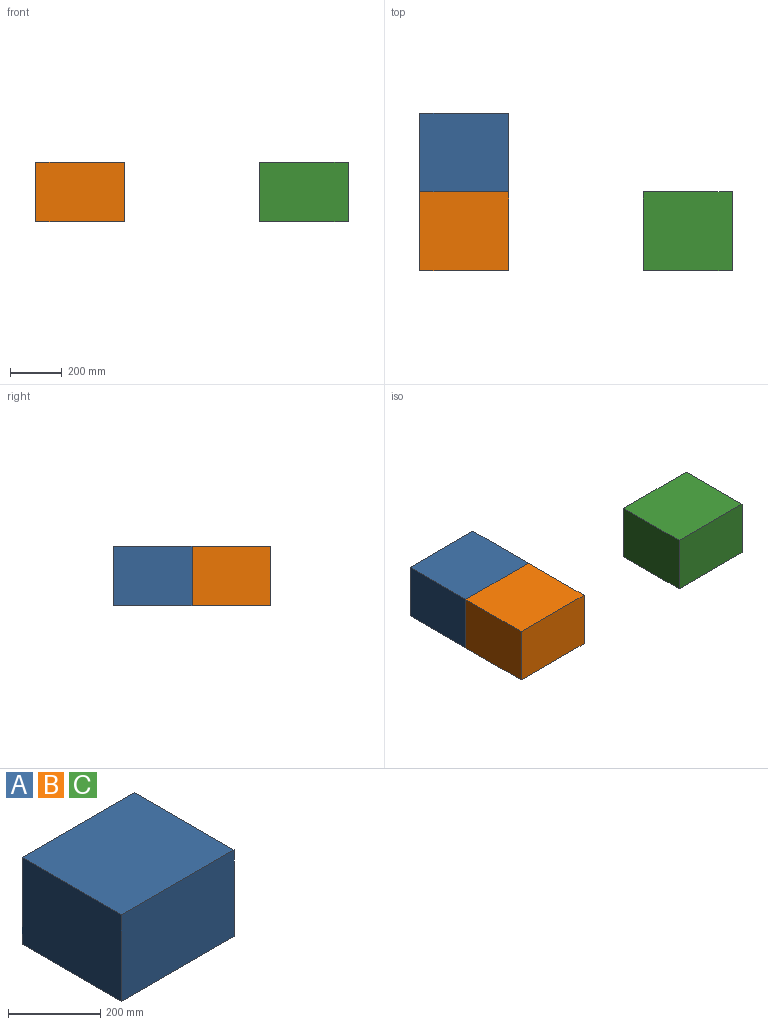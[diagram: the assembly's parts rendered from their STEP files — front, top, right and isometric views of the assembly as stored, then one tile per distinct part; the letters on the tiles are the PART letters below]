
ASSEMBLY  parts=3 mates=5
PART A: 6 faces, bbox 345x305x230 mm
  f0: plane 305x230mm, normal (-1,0,0), area 70150mm2, adj f1,f3,f4,f5
  f1: plane 345x230mm, normal (0,-1,0), area 79350mm2, adj f0,f2,f4,f5
  f2: plane 305x230mm, normal (1,0,0), area 70150mm2, adj f1,f3,f4,f5
  f3: plane 345x230mm, normal (0,1,0), area 79350mm2, adj f0,f2,f4,f5
  f4: plane 345x305mm, normal (0,0,1), area 105225mm2, adj f0,f1,f2,f3
  f5: plane 345x305mm, normal (0,0,-1), area 105225mm2, adj f0,f1,f2,f3
PART B: same geometry as A
PART C: same geometry as A
PLACE A t=(860.44,1794.7,-178.96)mm
PLACE B t=(860.44,1489.7,-178.96)mm
PLACE C t=(1726.91,1489.7,-178.96)mm
MATE planar A.f1 <-> B.f3  axis (0,-1,0) through (1205.44,1794.7,-178.96)mm
MATE slider C.f0 <-> B.f2  axis (-1,0,0) through (1726.91,1642.2,-63.96)mm
MATE planar B.f2 <-> A.f2  axis (1,0,0) through (1205.44,1642.2,-63.96)mm
MATE planar C.f4 <-> B.f4  axis (0,0,1) through (1899.41,1642.2,51.04)mm
MATE planar B.f4 <-> A.f4  axis (0,0,1) through (1032.94,1642.2,51.04)mm
